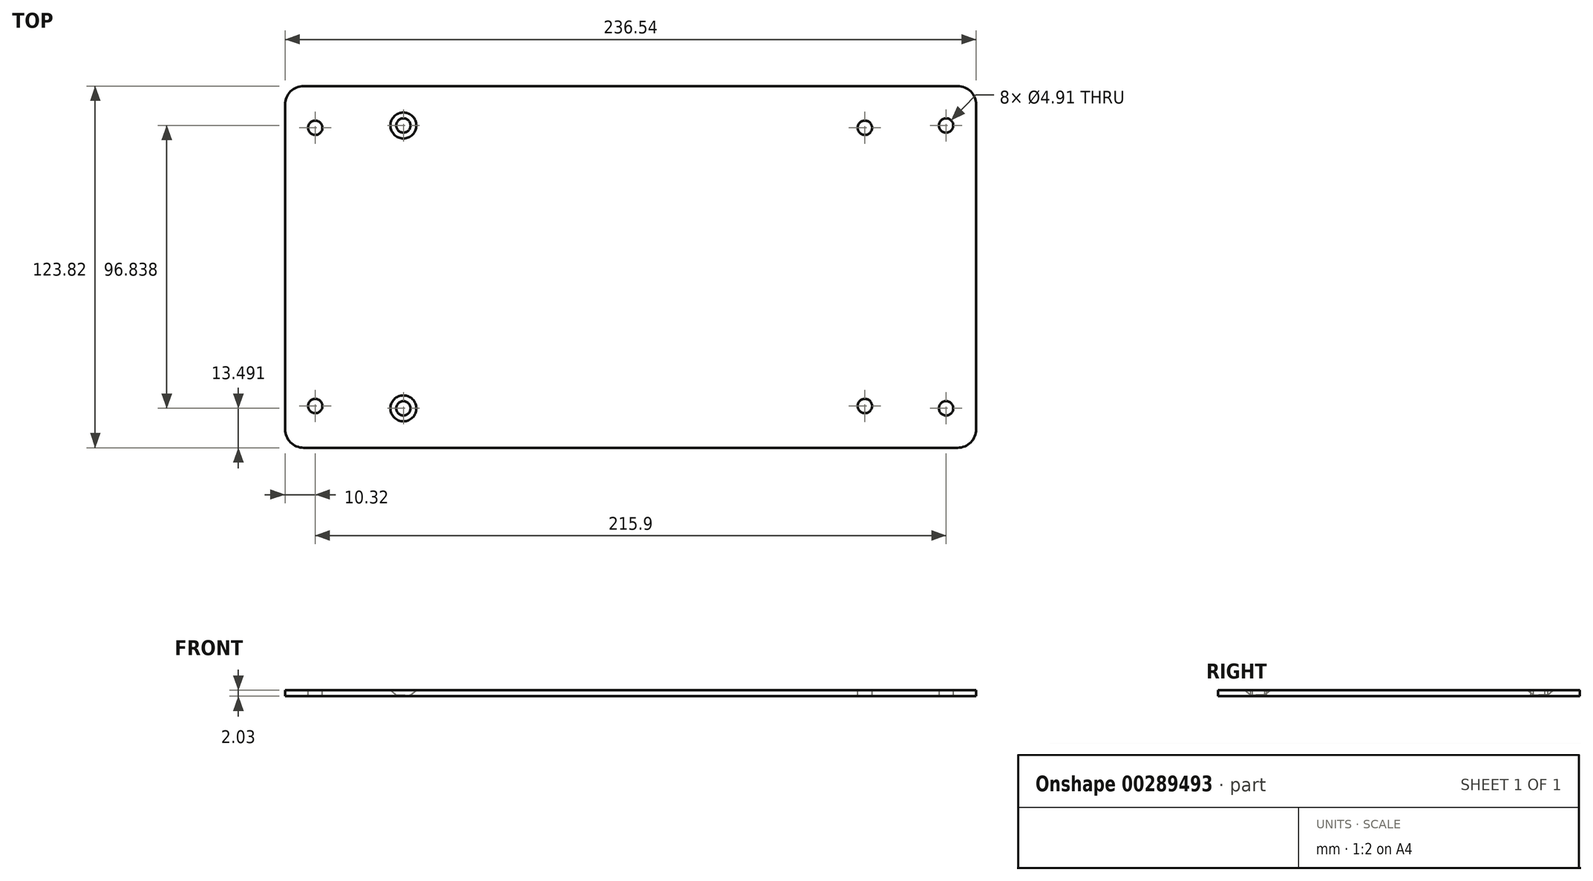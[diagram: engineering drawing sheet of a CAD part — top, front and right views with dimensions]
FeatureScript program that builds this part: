
annotation { "Feature Type Name" : "Feature", "Feature Type Description" : "" }
export const myFeature = defineFeature(function(context is Context, id is Id, definition is map)
    precondition{}
    {
        {
            var Q0;
            Q0=qCreatedBy(makeId("Top.planeOp"),FACE);
            var sketch = newSketch(context, id + "F0", { "sketchPlane" : qUnion([Q0])});
            skLineSegment(sketch, "E0.bottom", {"start": v(118.27, 61.91) * mm, "end": v(-118.27, 61.91) * mm});
            skLineSegment(sketch, "E0.top", {"start": v(118.27, -61.91) * mm, "end": v(-118.27, -61.91) * mm});
            skLineSegment(sketch, "E0.left", {"start": v(118.27, 61.91) * mm, "end": v(118.27, -61.91) * mm});
            skLineSegment(sketch, "E0.right", {"start": v(-118.27, 61.91) * mm, "end": v(-118.27, -61.91) * mm});
            skPoint(sketch, "E0.middle", {"position": v(0, 0) * mm});
            skPoint(sketch, "E1", {"position": v(107.95, 48.42) * mm});
            skLineSegment(sketch, "E2", {"start": v(107.95, 48.42) * mm, "end": v(107.95, -48.42) * mm, "construction": true});
            skPoint(sketch, "E3", {"position": v(107.95, 0) * mm});
            skLineSegment(sketch, "E4", {"start": v(118.27, 0) * mm, "end": v(-118.27, 0) * mm, "construction": true});
            skLineSegment(sketch, "E5", {"start": v(-77.79, 48.42) * mm, "end": v(-77.79, -48.42) * mm, "construction": true});
            skLineSegment(sketch, "E6", {"start": v(-107.95, 47.63) * mm, "end": v(-107.95, -47.63) * mm, "construction": true});
            skPoint(sketch, "E7", {"position": v(-107.95, 0) * mm});
            skLineSegment(sketch, "E8", {"start": v(80.17, 47.63) * mm, "end": v(80.17, -47.63) * mm, "construction": true});
            skSolve(sketch);
        }
        {
            var Q0;
            Q0 = qSketchRegion(id + "F0", true);
            extrude(context, id + "F1", {"entities" : qUnion([Q0]), "depth" : 2.03 * mm, "offsetDistance" : 25.4 * mm});
        }
        {
            var Q0;
            Q0=makeQuery(id+"F1.opExtrude","SWEPT_EDGE",EDGE,{"disambiguationData":[OSD([sQuery(id+"F0.wireOp",EDGE,"E0.top"),sQuery(id+"F0.wireOp",EDGE,"E0.left")])]});
            var Q1;
            Q1=makeQuery(id+"F1.opExtrude","SWEPT_EDGE",EDGE,{"disambiguationData":[OSD([sQuery(id+"F0.wireOp",EDGE,"E0.bottom"),sQuery(id+"F0.wireOp",EDGE,"E0.left")])]});
            var Q2;
            Q2=makeQuery(id+"F1.opExtrude","SWEPT_EDGE",EDGE,{"disambiguationData":[OSD([sQuery(id+"F0.wireOp",EDGE,"E0.top"),sQuery(id+"F0.wireOp",EDGE,"E0.right")])]});
            var Q3;
            Q3=makeQuery(id+"F1.opExtrude","SWEPT_EDGE",EDGE,{"disambiguationData":[OSD([sQuery(id+"F0.wireOp",EDGE,"E0.bottom"),sQuery(id+"F0.wireOp",EDGE,"E0.right")])]});
            fillet(context, id + "F2", {"entities" : qUnion([Q0, Q1, Q2, Q3]), "radius" : 6.35 * mm, "tangentPropagation" : true, "allowEdgeOverflow" : false});
        }
        {
            var Q0;
            Q0=sQuery(id+"F0.wireOp",VERTEX,"E6.start");
            var Q1;
            Q1=sQuery(id+"F0.wireOp",VERTEX,"E6.end");
            var Q2;
            Q2=sQuery(id+"F0.wireOp",VERTEX,"E8.end");
            var Q3;
            Q3=sQuery(id+"F0.wireOp",VERTEX,"E8.start");
            var Q4;
            Q4=makeQuery(id+"F1.opExtrude","SWEPT_BODY",BODY,{"disambiguationData":[OSD([sQuery(id+"F0.wireOp",EDGE,"E0.bottom"),sQuery(id+"F0.wireOp",EDGE,"E0.top"),sQuery(id+"F0.wireOp",EDGE,"E0.left"),sQuery(id+"F0.wireOp",EDGE,"E0.right")])]});
            hole(context, id + "F3", {"style" : HoleStyle.SIMPLE, "endStyle" : HoleEndStyle.THROUGH, "oppositeDirection" : true, "standardTappedOrClearance" : lookupTablePath({ "standard" : "ANSI", "size" : "#10 (0.2)", "type" : "Drilled" }), "standardBlindInLast" : lookupTablePath({ "standard" : "ANSI", "size" : "#10", "type" : "Drilled" }), "holeDiameter" : 4.9 * mm, "tappedDepth" : 12 * mm, "tapClearance" : 3, "locations" : qUnion([Q0, Q1, Q2, Q3]), "scope" : qUnion([Q4]), "startStyle" : HoleStartStyle.PART});
        }
        {
            var Q0;
            Q0=makeQuery(id+"F1.opExtrude","CAP_FACE",FACE,{"disambiguationData":[OSD([sQuery(id+"F0.wireOp",EDGE,"E0.bottom"),sQuery(id+"F0.wireOp",EDGE,"E0.top"),sQuery(id+"F0.wireOp",EDGE,"E0.left"),sQuery(id+"F0.wireOp",EDGE,"E0.right")])],"isStart":false});
            var sketch = newSketch(context, id + "F4", { "sketchPlane" : qUnion([Q0])});
            skPoint(sketch, "E9.0", {"position": v(-77.79, 48.42) * mm});
            skPoint(sketch, "E10.0", {"position": v(-77.79, -48.42) * mm});
            skPoint(sketch, "E11.0", {"position": v(107.95, -48.42) * mm});
            skPoint(sketch, "E12.0", {"position": v(107.95, 48.42) * mm});
            skSolve(sketch);
        }
        {
            var Q0;
            Q0=sQuery(id+"F4.wireOp",VERTEX,"E9.0");
            var Q1;
            Q1=sQuery(id+"F4.wireOp",VERTEX,"E10.0");
            var Q2;
            Q2=makeQuery(id+"F1.opExtrude","SWEPT_BODY",BODY,{"disambiguationData":[OSD([sQuery(id+"F0.wireOp",EDGE,"E0.bottom"),sQuery(id+"F0.wireOp",EDGE,"E0.top"),sQuery(id+"F0.wireOp",EDGE,"E0.left"),sQuery(id+"F0.wireOp",EDGE,"E0.right")])]});
            hole(context, id + "F5", {"style" : HoleStyle.C_SINK, "endStyle" : HoleEndStyle.THROUGH, "standardTappedOrClearance" : lookupTablePath({ "standard" : "ANSI", "size" : "#10 (0.2)", "type" : "Drilled" }), "standardBlindInLast" : lookupTablePath({ "standard" : "ANSI", "size" : "#10", "type" : "Drilled" }), "holeDiameter" : 4.9 * mm, "cSinkDiameter" : 8.9 * mm, "cSinkAngle" : 100 * degree, "tappedDepth" : 12 * mm, "tapClearance" : 3, "locations" : qUnion([Q0, Q1]), "scope" : qUnion([Q2]), "startStyle" : HoleStartStyle.PART});
        }
        {
            var Q0;
            Q0=sQuery(id+"F4.wireOp",VERTEX,"E12.0");
            var Q1;
            Q1=sQuery(id+"F4.wireOp",VERTEX,"E11.0");
            var Q2;
            Q2=makeQuery(id+"F1.opExtrude","SWEPT_BODY",BODY,{"disambiguationData":[OSD([sQuery(id+"F0.wireOp",EDGE,"E0.bottom"),sQuery(id+"F0.wireOp",EDGE,"E0.top"),sQuery(id+"F0.wireOp",EDGE,"E0.left"),sQuery(id+"F0.wireOp",EDGE,"E0.right")])]});
            hole(context, id + "F6", {"style" : HoleStyle.SIMPLE, "endStyle" : HoleEndStyle.THROUGH, "standardTappedOrClearance" : lookupTablePath({ "standard" : "ANSI", "size" : "#10 (0.2)", "type" : "Drilled" }), "standardBlindInLast" : lookupTablePath({ "standard" : "ANSI", "size" : "#10", "type" : "Drilled" }), "holeDiameter" : 4.9 * mm, "tappedDepth" : 12 * mm, "tapClearance" : 3, "locations" : qUnion([Q0, Q1]), "scope" : qUnion([Q2]), "startStyle" : HoleStartStyle.PART});
        }
    });
